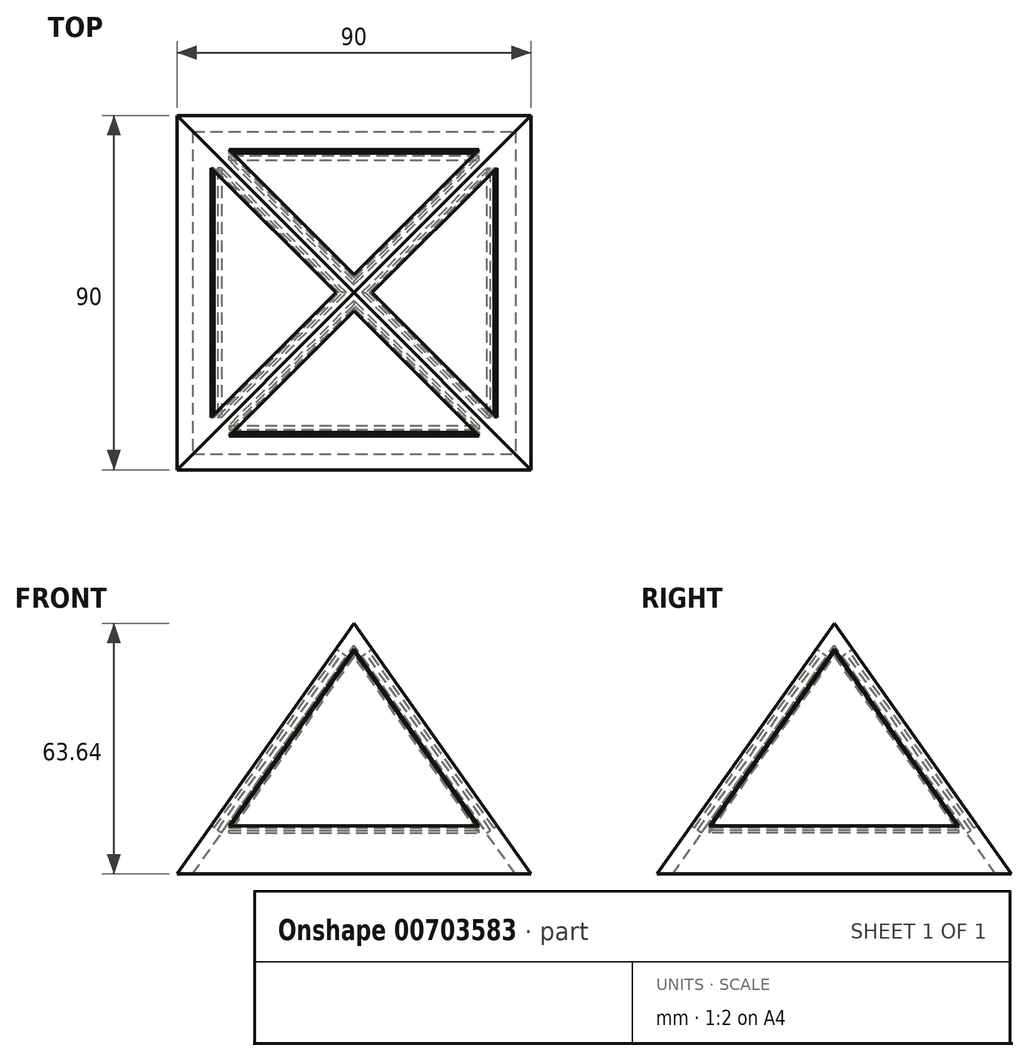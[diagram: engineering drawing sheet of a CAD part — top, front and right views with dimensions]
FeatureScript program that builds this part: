
annotation { "Feature Type Name" : "Feature", "Feature Type Description" : "" }
export const myFeature = defineFeature(function(context is Context, id is Id, definition is map)
    precondition{}
    {
        {
            assignVariable(context, id + "F0", {"name" : "Width", "anyValue" : 90});
        }
        {
            assignVariable(context, id + "F1", {"name" : "Hollow", "anyValue" : getVariable(context, 'Width') - 8});
        }
        {
            assignVariable(context, id + "F2", {"name" : "Paneldepth", "anyValue" : 1});
        }
        {
            var Q0;
            Q0=qCreatedBy(makeId("Top.planeOp"),FACE);
            var sketch = newSketch(context, id + "F3", { "sketchPlane" : qUnion([Q0])});
            skLineSegment(sketch, "E0.bottom", {"start": v(-45, 45) * mm, "end": v(45, 45) * mm});
            skLineSegment(sketch, "E0.top", {"start": v(-45, -45) * mm, "end": v(45, -45) * mm});
            skLineSegment(sketch, "E0.left", {"start": v(-45, 45) * mm, "end": v(-45, -45) * mm});
            skLineSegment(sketch, "E0.right", {"start": v(45, 45) * mm, "end": v(45, -45) * mm});
            skSolve(sketch);
        }
        {
            var Q0;
            Q0=makeQuery(id+"F3.imprint","IMPRINT",FACE,{"disambiguationData":[TD([[makeQuery(id+"F3.imprint","IMPRINT",EDGE,{"derivedFrom":sQuery(id+"F3.wireOp",EDGE,"E0.bottom")}),-1.0]])]});
            cPlane(context, id + "F4", {"entities" : qUnion([Q0]), "cplaneType" : CPlaneType.OFFSET, "offset" : (sqrt((sqrt((getVariable(context, 'Width') * getVariable(context, 'Width')) - ((getVariable(context, 'Width') / 2) * (getVariable(context, 'Width') / 2)))) * (sqrt((getVariable(context, 'Width') * getVariable(context, 'Width')) - ((getVariable(context, 'Width') / 2) * (getVariable(context, 'Width') / 2)))) - ((getVariable(context, 'Width') / 2) * (getVariable(context, 'Width') / 2)))) * mm, "width" : 150 * mm, "height" : 150 * mm});
        }
        {
            var Q0;
            Q0=qCreatedBy(id+"F4.planeOp",FACE);
            var sketch = newSketch(context, id + "F5", { "sketchPlane" : qUnion([Q0])});
            skPoint(sketch, "E1", {"position": v(0, 0) * mm});
            skSolve(sketch);
        }
        {
            var Q0;
            Q0=makeQuery(id+"F3.imprint","IMPRINT",FACE,{"disambiguationData":[TD([[makeQuery(id+"F3.imprint","IMPRINT",EDGE,{"derivedFrom":sQuery(id+"F3.wireOp",EDGE,"E0.bottom")}),-1.0]])]});
            var Q1;
            Q1=sQuery(id+"F5.wireOp",VERTEX,"E1");
            loft(context, id + "F6", {"sheetProfilesArray" : [{ "sheetProfileEntities" : qUnion([Q0]) }, { "sheetProfileEntities" : qUnion([Q1]) }]});
        }
        {
            var Q0;
            Q0=qCreatedBy(makeId("Top.planeOp"),FACE);
            cPlane(context, id + "F7", {"entities" : qUnion([Q0]), "cplaneType" : CPlaneType.OFFSET, "offset" : (sqrt((sqrt((getVariable(context, 'Hollow') * getVariable(context, 'Hollow')) - ((getVariable(context, 'Hollow') / 2) * (getVariable(context, 'Hollow') / 2)))) * (sqrt((getVariable(context, 'Hollow') * getVariable(context, 'Hollow')) - ((getVariable(context, 'Hollow') / 2) * (getVariable(context, 'Hollow') / 2)))) - ((getVariable(context, 'Hollow') / 2) * (getVariable(context, 'Hollow') / 2)))) * mm, "width" : 150 * mm, "height" : 150 * mm});
        }
        {
            var Q0;
            Q0=qCreatedBy(makeId("Top.planeOp"),FACE);
            var sketch = newSketch(context, id + "F8", { "sketchPlane" : qUnion([Q0])});
            skLineSegment(sketch, "E2.bottom", {"start": v(-41, 41) * mm, "end": v(41, 41) * mm});
            skLineSegment(sketch, "E2.top", {"start": v(-41, -41) * mm, "end": v(41, -41) * mm});
            skLineSegment(sketch, "E2.left", {"start": v(-41, 41) * mm, "end": v(-41, -41) * mm});
            skLineSegment(sketch, "E2.right", {"start": v(41, 41) * mm, "end": v(41, -41) * mm});
            skSolve(sketch);
        }
        {
            var Q0;
            Q0=qCreatedBy(id+"F7.planeOp",FACE);
            var sketch = newSketch(context, id + "F9", { "sketchPlane" : qUnion([Q0])});
            skPoint(sketch, "E3", {"position": v(0, 0) * mm});
            skSolve(sketch);
        }
        {
            var Q1;
            Q1=makeQuery(id+"F8.imprint","IMPRINT",FACE,{"disambiguationData":[TD([[makeQuery(id+"F8.imprint","IMPRINT",EDGE,{"derivedFrom":sQuery(id+"F8.wireOp",EDGE,"E2.bottom")}),-1.0]])]});
            var Q2;
            Q2=sQuery(id+"F9.wireOp",VERTEX,"E3");
            loft(context, id + "F10", {"operationType" : NewBodyOperationType.REMOVE, "sheetProfilesArray" : [{ "sheetProfileEntities" : qUnion([Q1]) }, { "sheetProfileEntities" : qUnion([Q2]) }]});
        }
        {
            var Q0;
            Q0=makeQuery(id+"F6.opLoft","SWEPT_FACE",FACE,{"disambiguationData":[OSD([sQuery(id+"F3.wireOp",EDGE,"E0.top"),sQuery(id+"F3.wireOp",EDGE,"E0.left"),sQuery(id+"F3.wireOp",EDGE,"E0.right")])]});
            cPlane(context, id + "F11", {"entities" : qUnion([Q0]), "cplaneType" : CPlaneType.OFFSET, "offset" : 0 * mm, "width" : 150 * mm, "height" : 150 * mm});
        }
        {
            var Q0;
            Q0=makeQuery(id+"F6.opLoft","SWEPT_FACE",FACE,{"disambiguationData":[OSD([sQuery(id+"F3.wireOp",EDGE,"E0.bottom"),sQuery(id+"F3.wireOp",EDGE,"E0.top"),sQuery(id+"F3.wireOp",EDGE,"E0.left")])]});
            cPlane(context, id + "F12", {"entities" : qUnion([Q0]), "cplaneType" : CPlaneType.OFFSET, "offset" : 0 * mm, "width" : 150 * mm, "height" : 150 * mm});
        }
        {
            var Q0;
            Q0=qCreatedBy(id+"F11.planeOp",FACE);
            var sketch = newSketch(context, id + "F13", { "sketchPlane" : qUnion([Q0])});
            skLineSegment(sketch, "E4", {"start": v(0, 43.96) * mm, "end": v(-31.72, -10.98) * mm});
            skLineSegment(sketch, "E5", {"start": v(-31.72, -10.98) * mm, "end": v(31.72, -10.98) * mm});
            skLineSegment(sketch, "E6", {"start": v(31.72, -10.98) * mm, "end": v(0, 43.96) * mm});
            skSolve(sketch);
        }
        {
            var Q0;
            Q0=qSketchRegion(id+"F13",true);
            extrude(context, id + "F14", {"entities" : qUnion([Q0]), "operationType" : NewBodyOperationType.REMOVE, "oppositeDirection" : true, "depth" : (getVariable(context, 'Paneldepth')) * mm, "offsetDistance" : 25 * mm});
        }
        {
            var Q0;
            Q0=qSketchRegion(id+"F13",true);
            extrude(context, id + "F15", {"entities" : qUnion([Q0]), "operationType" : NewBodyOperationType.REMOVE, "oppositeDirection" : true, "depth" : 5 * mm, "offsetDistance" : 25 * mm, "hasSecondDirection" : true, "secondDirectionOppositeDirection" : false, "secondDirectionDepth" : -2 * mm});
        }
        {
            var Q0;
            Q0=qCreatedBy(id+"F12.planeOp",FACE);
            var sketch = newSketch(context, id + "F16", { "sketchPlane" : qUnion([Q0])});
            skLineSegment(sketch, "E7", {"start": v(0, 43.96) * mm, "end": v(-31.72, -10.98) * mm});
            skLineSegment(sketch, "E8", {"start": v(-31.72, -10.98) * mm, "end": v(31.72, -10.98) * mm});
            skLineSegment(sketch, "E9", {"start": v(31.72, -10.98) * mm, "end": v(0, 43.96) * mm});
            skSolve(sketch);
        }
        {
            var Q0;
            Q0=qSketchRegion(id+"F16",true);
            extrude(context, id + "F17", {"entities" : qUnion([Q0]), "operationType" : NewBodyOperationType.REMOVE, "oppositeDirection" : true, "depth" : (getVariable(context, 'Paneldepth')) * mm, "offsetDistance" : 25 * mm});
        }
        {
            var Q0;
            Q0=qSketchRegion(id+"F16",true);
            extrude(context, id + "F18", {"entities" : qUnion([Q0]), "operationType" : NewBodyOperationType.REMOVE, "oppositeDirection" : true, "depth" : 5 * mm, "offsetDistance" : 25 * mm, "hasSecondDirection" : true, "secondDirectionOppositeDirection" : false, "secondDirectionDepth" : -2 * mm});
        }
        {
            var Q0;
            Q0=makeQuery(id+"F6.opLoft","SWEPT_FACE",FACE,{"disambiguationData":[OSD([sQuery(id+"F3.wireOp",EDGE,"E0.bottom"),sQuery(id+"F3.wireOp",EDGE,"E0.left"),sQuery(id+"F3.wireOp",EDGE,"E0.right")])]});
            var sketch = newSketch(context, id + "F19", { "sketchPlane" : qUnion([Q0])});
            skLineSegment(sketch, "E10", {"start": v(0, 43.96) * mm, "end": v(-31.72, -10.98) * mm});
            skLineSegment(sketch, "E11", {"start": v(-31.72, -10.98) * mm, "end": v(31.72, -10.98) * mm});
            skLineSegment(sketch, "E12", {"start": v(31.72, -10.98) * mm, "end": v(0, 43.96) * mm});
            skSolve(sketch);
        }
        {
            var Q0;
            Q0=qSketchRegion(id+"F19",true);
            extrude(context, id + "F20", {"entities" : qUnion([Q0]), "operationType" : NewBodyOperationType.REMOVE, "oppositeDirection" : true, "depth" : (getVariable(context, 'Paneldepth')) * mm, "offsetDistance" : 25 * mm});
        }
        {
            var Q0;
            Q0=qSketchRegion(id+"F19",true);
            extrude(context, id + "F21", {"entities" : qUnion([Q0]), "operationType" : NewBodyOperationType.REMOVE, "depth" : -5 * mm, "offsetDistance" : 25 * mm, "hasSecondDirection" : true, "secondDirectionOppositeDirection" : true, "secondDirectionDepth" : 2 * mm});
        }
        {
            var Q0;
            Q0=makeQuery(id+"F6.opLoft","SWEPT_FACE",FACE,{"disambiguationData":[OSD([sQuery(id+"F3.wireOp",EDGE,"E0.bottom"),sQuery(id+"F3.wireOp",EDGE,"E0.top"),sQuery(id+"F3.wireOp",EDGE,"E0.right")])]});
            var sketch = newSketch(context, id + "F22", { "sketchPlane" : qUnion([Q0])});
            skLineSegment(sketch, "E13", {"start": v(0, 43.96) * mm, "end": v(-31.72, -10.98) * mm});
            skLineSegment(sketch, "E14", {"start": v(-31.72, -10.98) * mm, "end": v(31.72, -10.98) * mm});
            skLineSegment(sketch, "E15", {"start": v(31.72, -10.98) * mm, "end": v(0, 43.96) * mm});
            skSolve(sketch);
        }
        {
            var Q0;
            Q0=qSketchRegion(id+"F22",true);
            extrude(context, id + "F23", {"entities" : qUnion([Q0]), "operationType" : NewBodyOperationType.REMOVE, "oppositeDirection" : true, "depth" : (getVariable(context, 'Paneldepth')) * mm, "offsetDistance" : 25 * mm});
        }
        {
            var Q0;
            Q0=qSketchRegion(id+"F22",true);
            extrude(context, id + "F24", {"entities" : qUnion([Q0]), "operationType" : NewBodyOperationType.REMOVE, "oppositeDirection" : true, "depth" : 5 * mm, "offsetDistance" : 25 * mm, "hasSecondDirection" : true, "secondDirectionOppositeDirection" : false, "secondDirectionDepth" : -2 * mm});
        }
    });
